# Revit family: Shower-Classic_Column-Four_Station-Acorn-Shower-Ware-646-TS-T25-GG-P-CA-SC-RD
name_source: partatom
category: Plumbing Fixtures
units: mm (PartAtom-declared; Revit-internal decimal feet)

## family parameters
Cut with Voids When Loaded = No
Host = Face
OmniClass Number = 23.45.05.14.17
OmniClass Title = Showers
Part Type = Normal
Room Calculation Point = No
Round Connector Dimension = Use Diameter
Shared = Yes

## types (1)
- 646-TS-T25-GG-P-CA-SC-RD
    4 Shower Stations = Yes
    6 - Air-Control, Single Temperature Metering = Yes
    6' Showerhead Discharge Height = Yes
    Assembly Code = D2090600
    CA - Ceiling Anchor Plate for Supply Cover = Yes
    CW Connection = Yes
    CWFU = 4
    Default Elevation = 0"
    Description = Classic Stainless Steel Column Shower
    Finish = Stainless Steel-Acorn-Type 304-Satin
    Finish- Other Components = Brass-Acorn-Chrome-Plated
    GG - Unit Shutoff Valve = Yes
    Grate Material = Metal-Acorn-Cast Iron
    HW Connection = Yes
    HWFU = 3
    Height = 76"
    Inlet Diameter = 3/4"
    Installation Instruction Link = https://www.acorneng.com
    Installation Type = Floor Mounted
    Manufacturer = Acorn Engineering
    Model = 646-TS-T25-GG-P-CA-SC-RD
    Outlet Diameter = 3/4"
    P - Penal Shower Head = Yes
    Product Documentation Link = https://www.acorneng.com
    Product Page URL = https://www.acorneng.com
    RD - Recessed Soap Dish = Yes
    SC - Supply Cover, Ceiling Height = Yes
    T25 - Clamping Collar, Vent Through Unit = Yes
    TS- Top Supply = Yes
    Tempered Water Connection = Yes
    URL = https://www.mgicontrols.com
    Vent Connection = Yes
    WFU = 3
    Waste Connection = Yes

## geometry (parser evidence)
native form markers: Sweep x8
no freeform markers — native parametric forms only
